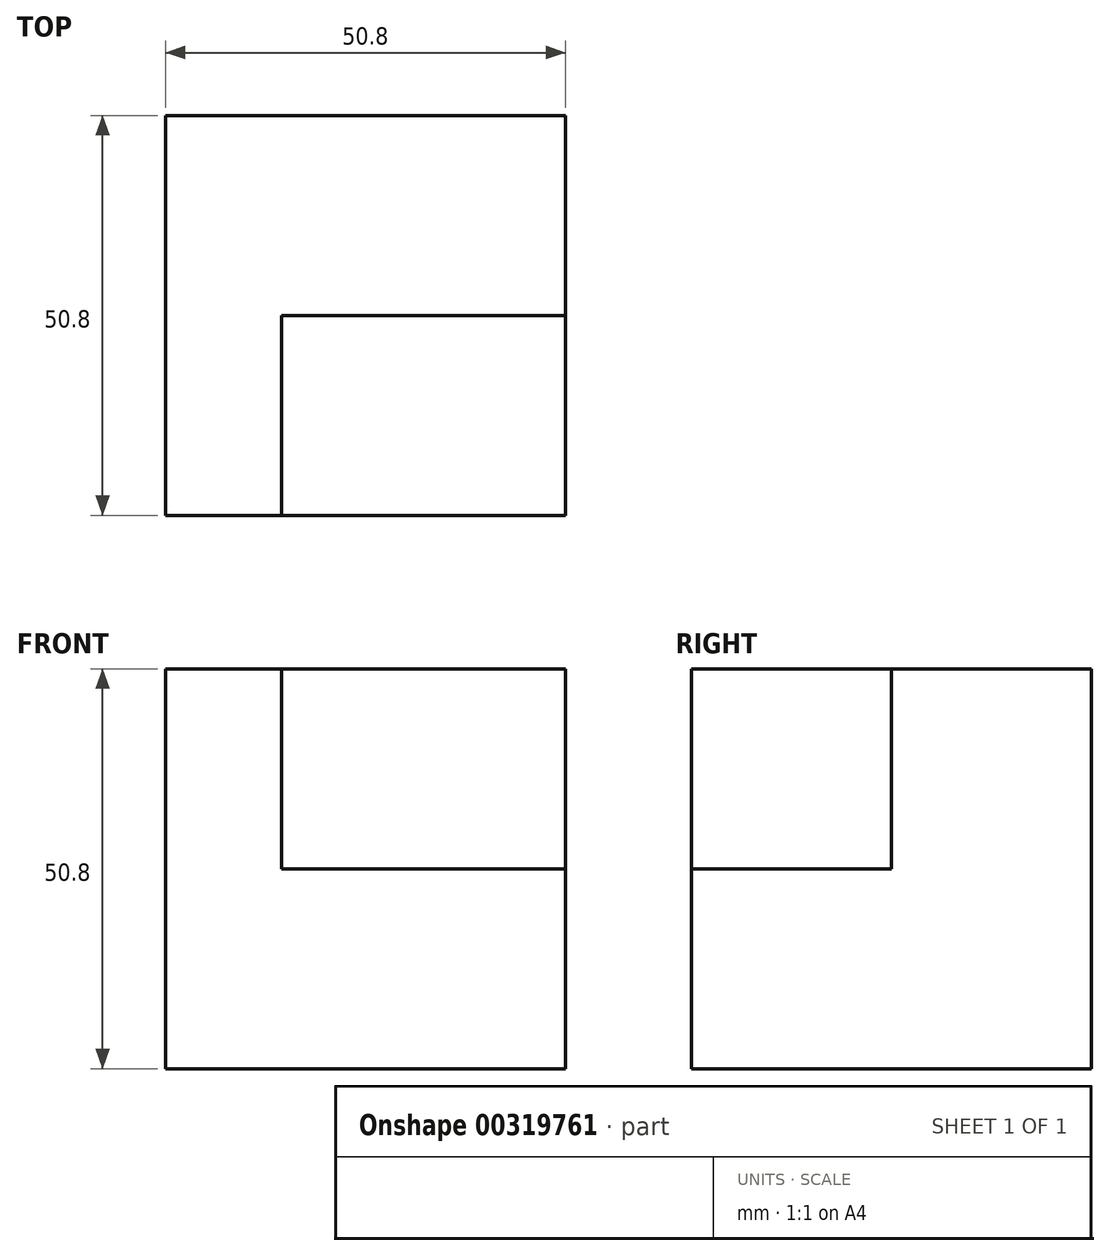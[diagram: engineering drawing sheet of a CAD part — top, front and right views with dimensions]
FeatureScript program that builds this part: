
annotation { "Feature Type Name" : "Feature", "Feature Type Description" : "" }
export const myFeature = defineFeature(function(context is Context, id is Id, definition is map)
    precondition{}
    {
        {
            var Q0;
            Q0=qCreatedBy(makeId("Right.planeOp"),FACE);
            var sketch = newSketch(context, id + "F0", { "sketchPlane" : qUnion([Q0])});
            skLineSegment(sketch, "E0", {"start": v(-26.8, 31.32) * mm, "end": v(24, 31.32) * mm});
            skLineSegment(sketch, "E1", {"start": v(24, -19.48) * mm, "end": v(24, 31.32) * mm});
            skLineSegment(sketch, "E2", {"start": v(24, -19.48) * mm, "end": v(-26.8, -19.48) * mm});
            skLineSegment(sketch, "E3", {"start": v(-26.8, -19.48) * mm, "end": v(-26.8, 31.32) * mm});
            skSolve(sketch);
        }
        {
            var Q0;
            Q0 = qSketchRegion(id + "F0", true);
            extrude(context, id + "F1", {"entities" : qUnion([Q0]), "depth" : 50.8 * mm});
        }
        {
            var Q0;
            Q0=makeQuery(id+"F1.opExtrude","SWEPT_FACE",FACE,{"disambiguationData":[OSD([sQuery(id+"F0.wireOp",EDGE,"E0")])]});
            var sketch = newSketch(context, id + "F2", { "sketchPlane" : qUnion([Q0])});
            skLineSegment(sketch, "E4.bottom", {"start": v(14.74, -26.8) * mm, "end": v(50.8, -26.8) * mm});
            skLineSegment(sketch, "E4.top", {"start": v(14.74, -1.4) * mm, "end": v(50.8, -1.4) * mm});
            skLineSegment(sketch, "E4.left", {"start": v(14.74, -26.8) * mm, "end": v(14.74, -1.4) * mm});
            skLineSegment(sketch, "E4.right", {"start": v(50.8, -26.8) * mm, "end": v(50.8, -1.4) * mm});
            skSolve(sketch);
        }
        {
            var Q0;
            Q0 = qSketchRegion(id + "F2", true);
            extrude(context, id + "F3", {"entities" : qUnion([Q0]), "operationType" : NewBodyOperationType.REMOVE, "oppositeDirection" : true, "depth" : 25.4 * mm});
        }
    });
